# Revit family: AISC Channel Shapes-Section
name_source: partatom
category: Detail Items
revit_build: Autodesk Revit Architecture 2012 (Build: 20110210_1515)
units: mm (PartAtom-declared; Revit-internal decimal feet)

## types (32) — shared parameters
Keynote = 05 12 00.B0

## per-type parameters (varying)
| type | A | W | bf | d | tf | tw | x |
| C15X50 | 0.1 SF | 50 | 0' - 3 23/32" | 1' - 3" | 0' - 0 21/32" | 0' - 0 23/32" | 0' - 0 13/16" |
| C15X40 | 0.08 SF | 40 | 0' - 3 17/32" | 1' - 3" | 0' - 0 21/32" | 0' - 0 17/32" | 0' - 0 25/32" |
| C15X33.9 | 0.07 SF | 33.9 | 0' - 3 13/32" | 1' - 3" | 0' - 0 21/32" | 0' - 0 13/32" | 0' - 0 25/32" |
| C12X30 | 0.06 SF | 30 | 0' - 3 5/32" | 1' - 0" | 0' - 0 1/2" | 0' - 0 1/2" | 0' - 0 11/16" |
| C12X25 | 0.05 SF | 25 | 0' - 3 1/16" | 1' - 0" | 0' - 0 1/2" | 0' - 0 3/8" | 0' - 0 11/16" |
| C12X20.7 | 0.04 SF | 20.7 | 0' - 2 15/16" | 1' - 0" | 0' - 0 1/2" | 0' - 0 9/32" | 0' - 0 11/16" |
| C10X30 | 0.06 SF | 30 | 0' - 3 1/32" | 0' - 10" | 0' - 0 7/16" | 0' - 0 11/16" | 0' - 0 21/32" |
| C10X25 | 0.05 SF | 25 | 0' - 2 7/8" | 0' - 10" | 0' - 0 7/16" | 0' - 0 17/32" | 0' - 0 5/8" |
| C10X20 | 0.04 SF | 20 | 0' - 2 3/4" | 0' - 10" | 0' - 0 7/16" | 0' - 0 3/8" | 0' - 0 19/32" |
| C10X15.3 | 0.03 SF | 15.3 | 0' - 2 19/32" | 0' - 10" | 0' - 0 7/16" | 0' - 0 1/4" | 0' - 0 5/8" |
| C9X20 | 0.04 SF | 20 | 0' - 2 21/32" | 0' - 9" | 0' - 0 13/32" | 0' - 0 7/16" | 0' - 0 19/32" |
| C9X15 | 0.03 SF | 15 | 0' - 2 1/2" | 0' - 9" | 0' - 0 13/32" | 0' - 0 9/32" | 0' - 0 19/32" |
| C9X13.4 | 0.03 SF | 13.4 | 0' - 2 7/16" | 0' - 9" | 0' - 0 13/32" | 0' - 0 7/32" | 0' - 0 19/32" |
| C8X18.7 | 0.04 SF | 18.7 | 0' - 2 17/32" | 0' - 8" | 0' - 0 3/8" | 0' - 0 1/2" | 0' - 0 9/16" |
| C8X18.5 - Obsolete | 0.04 SF | 18.75 | 0' - 2 17/32" | 0' - 8" | 0' - 0 3/8" | 0' - 0 1/2" | 0' - 0 9/16" |
| C8X13.7 | 0.03 SF | 13.7 | 0' - 2 11/32" | 0' - 8" | 0' - 0 3/8" | 0' - 0 5/16" | 0' - 0 9/16" |
| C8X11.5 | 0.02 SF | 11.5 | 0' - 2 1/4" | 0' - 8" | 0' - 0 3/8" | 0' - 0 7/32" | 0' - 0 9/16" |
| C7X14.7 | 0.03 SF | 14.7 | 0' - 2 5/16" | 0' - 7" | 0' - 0 3/8" | 0' - 0 13/32" | 0' - 0 17/32" |
| C7X12.2 | 0.03 SF | 12.2 | 0' - 2 3/16" | 0' - 7" | 0' - 0 3/8" | 0' - 0 5/16" | 0' - 0 17/32" |
| C7X9.8 | 0.02 SF | 9.8 | 0' - 2 3/32" | 0' - 7" | 0' - 0 3/8" | 0' - 0 7/32" | 0' - 0 17/32" |
| C6X13 | 0.03 SF | 13 | 0' - 2 5/32" | 0' - 6" | 0' - 0 11/32" | 0' - 0 7/16" | 0' - 0 1/2" |
| C6X10.5 | 0.02 SF | 10.5 | 0' - 2 1/32" | 0' - 6" | 0' - 0 11/32" | 0' - 0 5/16" | 0' - 0 1/2" |
| C6X8.2 | 0.02 SF | 8.2 | 0' - 1 29/32" | 0' - 6" | 0' - 0 11/32" | 0' - 0 3/16" | 0' - 0 1/2" |
| C5X9 | 0.02 SF | 9 | 0' - 1 7/8" | 0' - 5" | 0' - 0 5/16" | 0' - 0 5/16" | 0' - 0 15/32" |
| C5X6.7 | 0.01 SF | 6.7 | 0' - 1 3/4" | 0' - 5" | 0' - 0 5/16" | 0' - 0 3/16" | 0' - 0 15/32" |
| C4X7.2 | 0.01 SF | 7.2 | 0' - 1 23/32" | 0' - 4" | 0' - 0 9/32" | 0' - 0 5/16" | 0' - 0 15/32" |
| C4X5.4 | 0.01 SF | 5.4 | 0' - 1 19/32" | 0' - 4" | 0' - 0 9/32" | 0' - 0 3/16" | 0' - 0 15/32" |
| C4X4.5 | 0.01 SF | 4.5 | 0' - 1 19/32" | 0' - 4" | 0' - 0 9/32" | 0' - 0 1/8" | 0' - 0 1/2" |
| C3X6 | 0.01 SF | 6 | 0' - 1 19/32" | 0' - 3" | 0' - 0 9/32" | 0' - 0 11/32" | 0' - 0 15/32" |
| C3X5 | 0.01 SF | 5 | 0' - 1 1/2" | 0' - 3" | 0' - 0 9/32" | 0' - 0 1/4" | 0' - 0 7/16" |
| C3X4.1 | 0.01 SF | 4.1 | 0' - 1 13/32" | 0' - 3" | 0' - 0 9/32" | 0' - 0 5/32" | 0' - 0 7/16" |
| C3X3.5 | 0.01 SF | 3.5 | 0' - 1 3/8" | 0' - 3" | 0' - 0 9/32" | 0' - 0 1/8" | 0' - 0 7/16" |
